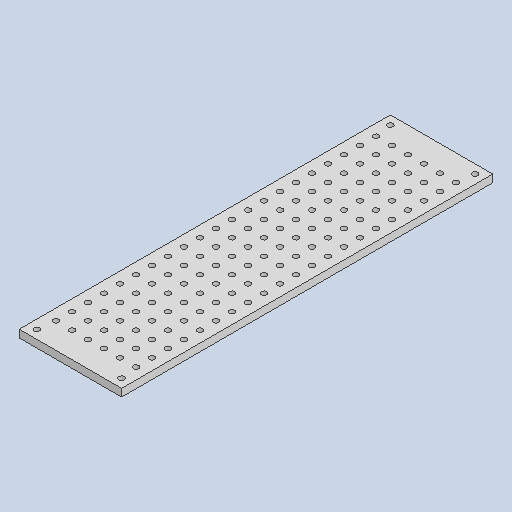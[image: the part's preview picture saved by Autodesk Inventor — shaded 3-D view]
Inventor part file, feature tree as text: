
AUTODESK INVENTOR PART (.ipt)
format: ipt  version: 2022.1 (Build 261234020, 234B)  size: 235,008 bytes
history: native  units: in
note: dims shown in document units (in); Inventor stores cm internally (conversion verified against a paired STEP export)
features: extrude x3, sketch x3, pattern_linear x1
ambient origin geometry x8: Origin, YZ Plane, XZ Plane, XY Plane, X Axis, Y Axis, Z Axis, Center Point
bodies: Solid1 (feature_tree)
feature tree (7):
  extrude  "Extrusion1"  Depth=11.6in
  extrude  "Extrusion2"  Depth=0.2362in
  extrude  "Extrusion3"  Depth=0.2756in
  pattern_linear  "Rectangular Pattern1"  Spacing1=0.1772in  [1 undecoded]
  sketch  "Sketch1"  dims[d0=3.2in d1=11.6in]
  sketch  "Sketch2"  dims[d2=0.2362in d3=0.0in d4=0.1772in]
  sketch  "Sketch3"  dims[d6=0.2756in d7=0.2756in d8=0.1772in d9=0.2756in d10=0.2756in d11=0.1772in d12=0.2756in d13=0.2756in d14=0.1772in d15=0.2756in d16=0.2756in d17=1.0in d18=0.0in d19=0.1772in d20=0.35in d22=0.1181in d23=0.0in d24=2.3622in d26=0.5in d27=8.2677in d29=0.5in d64=0.8in]
note: 1 required parameter value undecoded (feature->parameter linkage not recoverable at this tier; creation-order binding heuristic only, values carry confidence <= 0.55)
